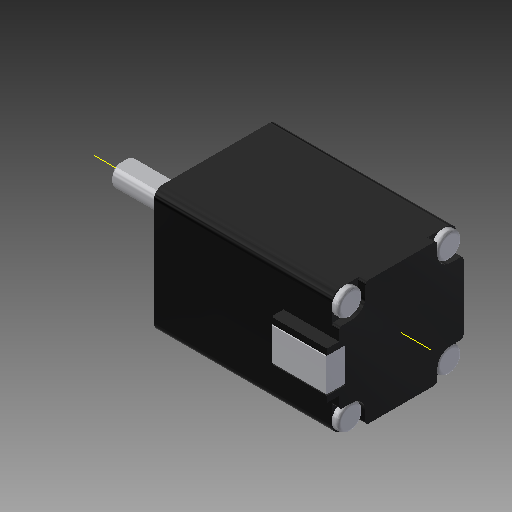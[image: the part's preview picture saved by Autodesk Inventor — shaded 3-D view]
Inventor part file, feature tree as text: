
AUTODESK INVENTOR PART (.ipt)
format: ipt  version: 2019 (Build 230136000, 136)  size: 436,736 bytes
history: native  units: mm
features: sketch x12, extrude x11, projected_geometry x6, chamfer x4, fillet x4, hole x1, other x1, pattern_circular x1
ambient origin geometry x8: Origin, YZ Plane, XZ Plane, XY Plane, X Axis, Y Axis, Z Axis, Center Point
bodies: Body1 (feature_tree)
feature tree (40):
  extrude  "Extrusion3"  Depth=20.1mm
  hole  "Hole1"  [1 undecoded]
  chamfer  "Chamfer1"  Distance=40.0mm Angle=360.0deg
  extrude  "Extrusion4"  Depth=2.0mm TaperAngle=45.0deg
  fillet  "Fillet1"  Radius=15.0mm
  extrude  "Extrusion5"  Depth=0.15mm
  extrude  "Extrusion6"  Depth=13.5mm TaperAngle=0.0deg
  chamfer  "Chamfer2"  Distance=12.0mm
  extrude  "Extrusion7"  Depth=9.0mm
  chamfer  "Chamfer3"  Distance=0.5mm
  extrude  "Extrusion8"  Depth=2.0mm
  extrude  "Extrusion9"  Depth=2.2mm
  fillet  "Fillet3"  Radius=2.2mm
  other  "Work Axis1"
  pattern_circular  "Circular Pattern2"  [2 undecoded]
  fillet  "Fillet4"  Radius=4.1mm
  extrude  "Extrusion10"  Depth=1.0mm TaperAngle=0.0deg
  chamfer  "Chamfer4"  Distance=0.5mm
  extrude  "Extrusion11"  Depth=0.1mm TaperAngle=360.0deg
  extrude  "Extrusion12"  Depth=0.5mm
  fillet  "Fillet5"  Radius=9.0mm
  extrude  "Extrusion13"  Depth=1.0mm
  sketch  "Sketch1"  dims[d2=20.1mm d3=20.1mm]
  sketch  "Sketch4"  dims[d4=1.5mm d5=2.1mm]
  projected_geometry  "Projected Loop2"
  sketch  "Sketch5"  dims[d6=8.0mm d7=40.0mm d9=360.0deg]
  sketch  "Sketch6"  dims[d15=30.0mm d16=0.0mm]
  sketch  "Sketch7"  dims[d17=1.567mm d18=4.0mm d19=4.0mm d20=2.0mm d21=90.0deg d22=3.5mm d23=20.594885mm d24=0.25mm d25=2.0mm d26=45.0deg d27=15.0mm]
  projected_geometry  "Projected Loop3"
  sketch  "Sketch8"  dims[d28=1.5mm d29=0.0mm d30=0.15mm]
  sketch  "Sketch9"  dims[d31=4.0mm d32=13.5mm d33=0.0mm]
  projected_geometry  "Projected Loop4"
  sketch  "Sketch10"  dims[d35=3.5mm]
  sketch  "Sketch12"  dims[d36=90.0deg d37=12.0mm d38=0.0mm]
  sketch  "Sketch13"  dims[d39=0.25mm d40=2.0mm d41=45.0deg d42=9.0mm d43=0.5mm d44=0.0mm]
  projected_geometry  "Projected Loop5"
  sketch  "Sketch14"  dims[d45=0.25mm d46=2.0mm d47=45.0deg d48=4.0mm]
  projected_geometry  "Projected Loop6"
  sketch  "Sketch15"  dims[d49=2.2mm d50=2.2mm d51=2.2mm d52=1.2mm d53=0.0mm d55=4.1mm d56=1.0mm d57=0.0mm d58=0.5mm d62=40.0mm d63=360.0deg d65=0.5mm d66=9.0mm d67=1.0mm d68=2.8mm d69=2.0mm d70=0.0mm d71=0.25mm d72=2.0mm d73=45.0deg d74=1.0mm d75=4.0mm d76=0.0mm d77=0.1mm d79=0.1mm d80=8.95mm d81=0.0mm d82=0.1mm d83=0.1mm d84=0.0mm]
  projected_geometry  "Projected Loop7"
note: 3 required parameter values undecoded (feature->parameter linkage not recoverable at this tier; creation-order binding heuristic only, values carry confidence <= 0.55)
